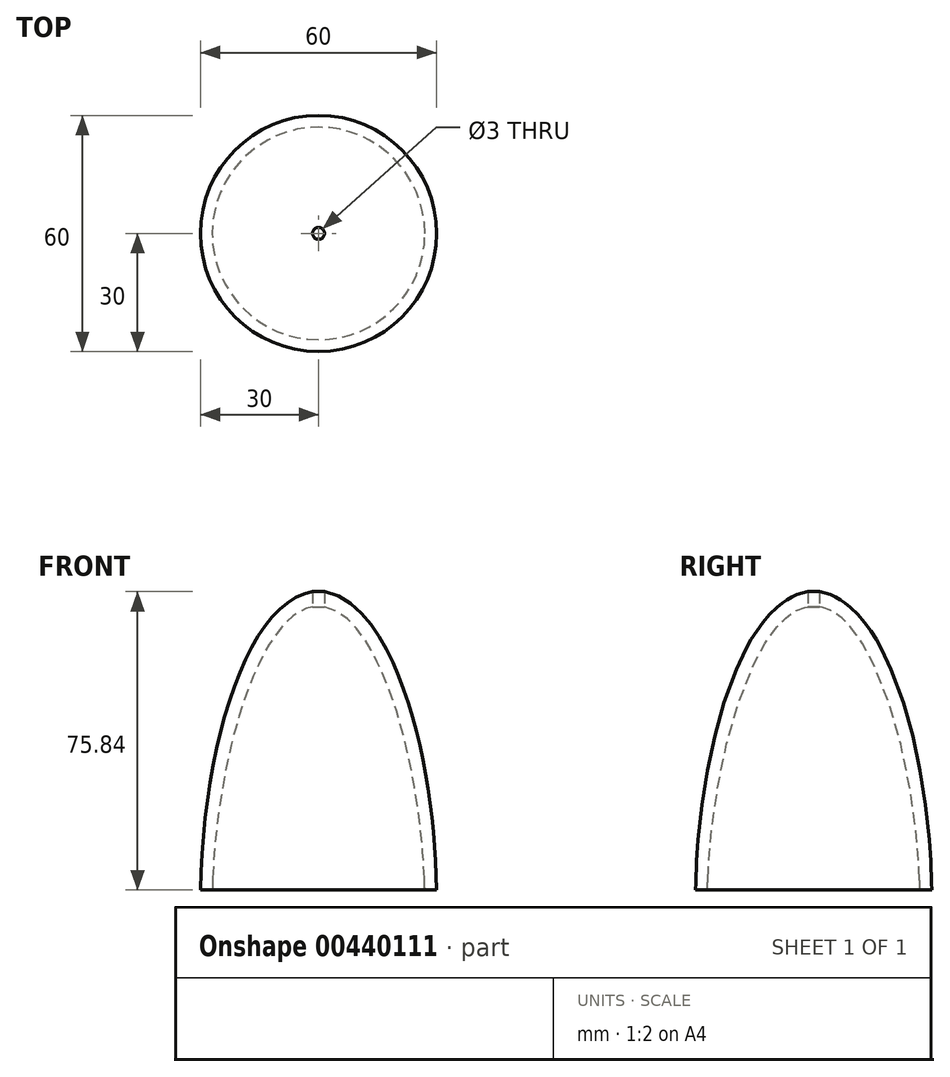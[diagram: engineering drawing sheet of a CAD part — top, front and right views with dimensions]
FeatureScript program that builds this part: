
annotation { "Feature Type Name" : "Feature", "Feature Type Description" : "" }
export const myFeature = defineFeature(function(context is Context, id is Id, definition is map)
    precondition{}
    {
        {
            var Q0;
            Q0=qCreatedBy(makeId("Front.planeOp"),FACE);
            var sketch = newSketch(context, id + "F0", { "sketchPlane" : qUnion([Q0])});
            skLineSegment(sketch, "E0", {"start": v(27, 0) * mm, "end": v(30, 0) * mm});
            skFitSpline(sketch, "E1", {"points": [v(0, 76) * mm, v(30, 0) * mm], "startDerivative": vector(54.64, -2.71) * mm, "endDerivative": vector(1.87, -108) * mm});
            skLineSegment(sketch, "E2", {"start": v(0, 0) * mm, "end": v(0, 72) * mm, "construction": true});
            skLineSegment(sketch, "E3", {"start": v(0, 72) * mm, "end": v(0, 76) * mm});
            skFitSpline(sketch, "E4", {"points": [v(0, 72) * mm, v(27, 0) * mm], "startDerivative": vector(41.76, 1.85) * mm, "endDerivative": vector(3.1, -108.7) * mm});
            skLineSegment(sketch, "E5", {"start": v(0, 0) * mm, "end": v(24, 0) * mm, "construction": true});
            skLineSegment(sketch, "E6", {"start": v(27, 0) * mm, "end": v(27, -30) * mm});
            skLineSegment(sketch, "E7", {"start": v(27, -30) * mm, "end": v(0, -30) * mm});
            skLineSegment(sketch, "E8", {"start": v(24, 0) * mm, "end": v(24, -25) * mm});
            skLineSegment(sketch, "E9", {"start": v(24, -25) * mm, "end": v(0, -25) * mm});
            skLineSegment(sketch, "E10", {"start": v(24, 0) * mm, "end": v(24, 3) * mm});
            skLineSegment(sketch, "E11", {"start": v(24, 3) * mm, "end": v(26.89, 3) * mm});
            skLineSegment(sketch, "E12", {"start": v(0, -25) * mm, "end": v(0, -30) * mm});
            skSolve(sketch);
        }
        {
            var Q0;
            Q0=makeQuery(id+"F0.imprint","IMPRINT",FACE,{"disambiguationData":[TD([[makeQuery(id+"F0.imprint","IMPRINT",EDGE,{"derivedFrom":sQuery(id+"F0.wireOp",EDGE,"E0")}),1.0]])]});
            var Q1;
            Q1=sQuery(id+"F0.wireOp",EDGE,"E2");
            revolve(context, id + "F1", {"entities" : qUnion([Q0]), "axis" : qUnion([Q1]), "revolveType" : RevolveType.FULL});
        }
        {
            var Q0;
            Q0=qCreatedBy(makeId("Top.planeOp"),FACE);
            cPlane(context, id + "F2", {"entities" : qUnion([Q0]), "cplaneType" : CPlaneType.OFFSET, "offset" : 30 * mm, "oppositeDirection" : true, "width" : 150 * mm, "height" : 150 * mm});
        }
        {
            var Q0;
            Q0=qCreatedBy(id+"F2.planeOp",FACE);
            var sketch = newSketch(context, id + "F3", { "sketchPlane" : qUnion([Q0])});
            skCircle(sketch, "E13", {"center": v(0, 0) * mm, "radius": 1 * mm});
            skSolve(sketch);
        }
        {
            var Q0;
            Q0=sQuery(id+"F3.wireOp",VERTEX,"E13.center");
            var Q1;
            Q1=makeQuery(id+"F1.opRevolve","SWEPT_BODY",BODY,{"disambiguationData":[OSD([sQuery(id+"F0.wireOp",EDGE,"E0"),sQuery(id+"F0.wireOp",EDGE,"E1"),sQuery(id+"F0.wireOp",EDGE,"E3"),sQuery(id+"F0.wireOp",EDGE,"E4"),sQuery(id+"F0.wireOp",EDGE,"E6"),sQuery(id+"F0.wireOp",EDGE,"E7"),sQuery(id+"F0.wireOp",EDGE,"E8"),sQuery(id+"F0.wireOp",EDGE,"E9"),sQuery(id+"F0.wireOp",EDGE,"E10"),sQuery(id+"F0.wireOp",EDGE,"E11"),sQuery(id+"F0.wireOp",EDGE,"E12")])]});
            hole(context, id + "F4", {"style" : HoleStyle.SIMPLE, "endStyle" : HoleEndStyle.BLIND, "oppositeDirection" : true, "holeDiameter" : 3 * mm, "majorDiameter" : 5 * mm, "holeDepth" : 12 * mm, "isTappedThrough" : true, "tappedDepth" : 12 * mm, "tapClearance" : 3, "locations" : qUnion([Q0]), "scope" : qUnion([Q1])});
        }
    });
